# Revit family: pfav-p80_1600dmj1_50Hz.
name_source: partatom
category: 機械設備
units: mm (PartAtom-declared; Revit-internal decimal feet)

## family parameters
OmniClass タイトル = Split System Air Conditioning Units
OmniClass 番号 = 23.75.10.24.21.27.27
パーツ タイプ = 標準
ロード時にボイドで切り取り = いいえ
丸型コネクタ寸法 = 直径を使用
作業面ベース = いいえ
共有 = いいえ
常に垂直 = はい
部屋計算ポイント = いいえ

## types (11) — shared parameters
Clearance Back = 50  [stored 0.164042 ft]
Clearance Right = 100  [stored 0.328084 ft]
Clearance Top = 1000  [stored 3.28084 ft]
IfcExportAs = IfcUnitaryEquipmentType
IfcExportType = AIRCONDITIONINGUNIT
OmniClassCode = 23-33 17 13 11
S寸法 = 150
URL = https://www.mitsubishielectric.co.jp
Uniclass2015Code = Pr_70_65_03_84
Uniclass2015Title = Split coil remote air cooled condensing units
Uniclass2015Version = Systems v1.9
サービススペース = はい
仕様書バージョン = Version1.0
企業コード = 108420
冷媒管径 = 100.00 mm
冷媒高低圧ガス管径 = 0.00 mm
分類コード = 50053003023020
加湿給水管径 = 27.00 mm
参照している仕様書等のバージョン = 公共建築工事標準仕様書（機械設備工事編）平成31年度版
周波数 = 50 Hz
呼称 = パッケージ形空気調和機_室内機
始動方式 = 直入
形式 = 床置（露出）立形
本体マテリアル = <カテゴリ別>
極数 = 3
機外静圧 = 30.0 Pa
法定耐用年数 = 15
消費電力_加湿器 = 0 W
消費電力_電気ヒーター = 0 W
相 = 3
相_電気ヒーター = 1
積算_科目 = 1 空気調和設備
符号 = PAC-FRV(J)
製品リリース年月 = 2017年4月18日
製品出荷対象 = 国内
製造元 = 三菱電機株式会社
設置方法 = 床置形
説明 = 設備用パッケージエアコン 空冷床置形・冷暖兼用 ファシレアＤＤ
負荷分類 = 3_ファン類
運転質量 = 0.00 kg
電動機出力_圧縮機 = 0 W
電圧 = 200 V
電圧_電気ヒーター = 0 V
zero-valued in all types: APF, COP, 価格, 有効加湿量, 機械基礎_D, 機械基礎_H, 機械基礎_W

## per-type parameters (varying)
- PFAV-P80DMJ1: Clearance Front=800  [stored 2.62467 ft]; Clearance Left=500  [stored 1.64042 ft]; Depth=485  [stored 1.59121 ft]; Height=1730  [stored 5.67585 ft]; MAX風量=1620.0 m³/h; Width=760; ダクト幅=383 mm; ダクト高=334 mm; ドレン管径=34.00 mm; 冷媒ガス管径=15.88 mm; 冷媒液管径=9.52 mm; 冷媒管径符号=Bd; 冷房能力=7 kW; 形名=PFAV-P-DMJ : PFAV-P80DMJ1; 推奨ブレーカー容量=15 A; 暖房能力=8 kW; 最大電流値=5 A; 最小電線太さ_mm2=1.6; 消費電力=150 W; 消費電力_冷房=150 W; 消費電力_暖房=150 W; 製品質量=121.00 kg; 質量=145.20 kg; 電動機出力_送風機=1200 W; 音響パワーレベル(dB)=61; 風量=1620.0 m³/h; 風量（m3／min）=27
- PFAV-P280DMJ1: Clearance Front=800  [stored 2.62467 ft]; Clearance Left=500  [stored 1.64042 ft]; Depth=485  [stored 1.59121 ft]; Height=1730  [stored 5.67585 ft]; MAX風量=5400.0 m³/h; Width=980  [stored 3.21522 ft]; ダクト幅=715 mm; ダクト高=334 mm; ドレン管径=34.00 mm; 冷媒ガス管径=22.20 mm; 冷媒液管径=9.52 mm; 冷媒管径符号=Bf; 冷房能力=25 kW; 形名=PFAV-P-DMJ : PFAV-P280DMJ1; 推奨ブレーカー容量=15 A; 暖房能力=28 kW; 最大電流値=6 A; 最小電線太さ_mm2=1.6; 消費電力=1150 W; 消費電力_冷房=1150 W; 消費電力_暖房=1150 W; 製品質量=140.00 kg; 質量=168.00 kg; 電動機出力_送風機=1200 W; 音響パワーレベル(dB)=76; 風量=5400.0 m³/h; 風量（m3／min）=90
- PFAV-P450DMJ1: Clearance Front=1000  [stored 3.28084 ft]; Clearance Left=100  [stored 0.328084 ft]; Depth=635; Height=1897  [stored 6.22375 ft]; MAX風量=8400.0 m³/h; Width=1200; ダクト幅=1046 mm; ダクト高=489 mm; ドレン管径=34.00 mm; 冷媒ガス管径=28.58 mm; 冷媒液管径=15.88 mm; 冷媒管径符号=Dh; 冷房能力=40 kW; 形名=PFAV-P-DMJ : PFAV-P450DMJ1; 推奨ブレーカー容量=15 A; 暖房能力=45 kW; 最大電流値=10 A; 最小電線太さ_mm2=1.6; 消費電力=1310 W; 消費電力_冷房=1310 W; 消費電力_暖房=1310 W; 製品質量=240.00 kg; 質量=288.00 kg; 電動機出力_送風機=2400 W; 音響パワーレベル(dB)=75; 風量=8400.0 m³/h; 風量（m3／min）=140
- PFAV-P140DMJ1: Clearance Front=800  [stored 2.62467 ft]; Clearance Left=500  [stored 1.64042 ft]; Depth=485  [stored 1.59121 ft]; Height=1730  [stored 5.67585 ft]; MAX風量=2700.0 m³/h; Width=760; ダクト幅=383 mm; ダクト高=334 mm; ドレン管径=34.00 mm; 冷媒ガス管径=15.88 mm; 冷媒液管径=9.52 mm; 冷媒管径符号=Bd; 冷房能力=13 kW; 形名=PFAV-P-DMJ : PFAV-P140DMJ1; 推奨ブレーカー容量=15 A; 暖房能力=14 kW; 最大電流値=5 A; 最小電線太さ_mm2=1.6; 消費電力=410 W; 消費電力_冷房=410 W; 消費電力_暖房=410 W; 製品質量=136.00 kg; 質量=163.20 kg; 電動機出力_送風機=1200 W; 音響パワーレベル(dB)=68; 風量=2700.0 m³/h; 風量（m3／min）=45
- PFAV-P224DMJ1: Clearance Front=800  [stored 2.62467 ft]; Clearance Left=500  [stored 1.64042 ft]; Depth=485  [stored 1.59121 ft]; Height=1730  [stored 5.67585 ft]; MAX風量=3900.0 m³/h; Width=980  [stored 3.21522 ft]; ダクト幅=715 mm; ダクト高=334 mm; ドレン管径=34.00 mm; 冷媒ガス管径=19.05 mm; 冷媒液管径=9.52 mm; 冷媒管径符号=Be; 冷房能力=20 kW; 形名=PFAV-P-DMJ : PFAV-P224DMJ1; 推奨ブレーカー容量=15 A; 暖房能力=22 kW; 最大電流値=6 A; 最小電線太さ_mm2=1.6; 消費電力=510 W; 消費電力_冷房=510 W; 消費電力_暖房=510 W; 製品質量=136.00 kg; 質量=163.20 kg; 電動機出力_送風機=1200 W; 音響パワーレベル(dB)=68; 風量=3900.0 m³/h; 風量（m3／min）=65
- PFAV-P560DMJ1: Clearance Front=1000  [stored 3.28084 ft]; Clearance Left=100  [stored 0.328084 ft]; Depth=635; Height=1897  [stored 6.22375 ft]; MAX風量=9900.0 m³/h; Width=1200; ダクト幅=1046 mm; ダクト高=489 mm; ドレン管径=34.00 mm; 冷媒ガス管径=28.58 mm; 冷媒液管径=15.88 mm; 冷媒管径符号=Dh; 冷房能力=50 kW; 形名=PFAV-P-DMJ : PFAV-P560DMJ1; 推奨ブレーカー容量=15 A; 暖房能力=56 kW; 最大電流値=10 A; 最小電線太さ_mm2=1.6; 消費電力=1690 W; 消費電力_冷房=1690 W; 消費電力_暖房=1690 W; 製品質量=240.00 kg; 質量=288.00 kg; 電動機出力_送風機=2400 W; 音響パワーレベル(dB)=78; 風量=9900.0 m³/h; 風量（m3／min）=165
- PFAV-P670DMJ1: Clearance Front=1000  [stored 3.28084 ft]; Clearance Left=100  [stored 0.328084 ft]; Depth=1064  [stored 3.49081 ft]; Height=1830  [stored 6.00394 ft]; MAX風量=12600.0 m³/h; Width=1750  [stored 5.74147 ft]; ダクト幅=677 mm; ダクト高=484 mm; ドレン管径=42.70 mm; 冷媒ガス管径=28.58 mm; 冷媒液管径=15.88 mm; 冷媒管径符号=Dh; 冷房能力=63 kW; 形名=PFAV-P-DMJ : PFAV-P670DMJ1; 推奨ブレーカー容量=40 A; 暖房能力=63 kW; 最大電流値=21 A; 最小電線太さ_mm2=5.5; 消費電力=2140 W; 消費電力_冷房=2140 W; 消費電力_暖房=2140 W; 製品質量=418.00 kg; 質量=501.60 kg; 電動機出力_送風機=7500 W; 音響パワーレベル(dB)=77; 風量=12600.0 m³/h; 風量（m3／min）=210
- PFAV-P800DMJ1: Clearance Front=1000  [stored 3.28084 ft]; Clearance Left=100  [stored 0.328084 ft]; Depth=1064  [stored 3.49081 ft]; Height=1830  [stored 6.00394 ft]; MAX風量=15600.0 m³/h; Width=1750  [stored 5.74147 ft]; ダクト幅=677 mm; ダクト高=484 mm; ドレン管径=42.70 mm; 冷媒ガス管径=31.75 mm; 冷媒液管径=19.05 mm; 冷媒管径符号=Ei; 冷房能力=71 kW; 形名=PFAV-P-DMJ : PFAV-P800DMJ1; 推奨ブレーカー容量=40 A; 暖房能力=80 kW; 最大電流値=21 A; 最小電線太さ_mm2=5.5; 消費電力=3640 W; 消費電力_冷房=3640 W; 消費電力_暖房=3640 W; 製品質量=424.00 kg; 質量=508.80 kg; 電動機出力_送風機=7500 W; 音響パワーレベル(dB)=82; 風量=15600.0 m³/h; 風量（m3／min）=260
- PFAV-P1120DMJ1: Clearance Front=1000  [stored 3.28084 ft]; Clearance Left=100  [stored 0.328084 ft]; Depth=1064  [stored 3.49081 ft]; Height=1830  [stored 6.00394 ft]; MAX風量=20400.0 m³/h; Width=1750  [stored 5.74147 ft]; ダクト幅=677 mm; ダクト高=484 mm; ドレン管径=42.70 mm; 冷媒ガス管径=38.10 mm; 冷媒液管径=19.05 mm; 冷媒管径符号=Ek; 冷房能力=100 kW; 形名=PFAV-P-DMJ : PFAV-P1120DMJ1; 推奨ブレーカー容量=50 A; 暖房能力=112 kW; 最大電流値=32 A; 最小電線太さ_mm2=8; 消費電力=5960 W; 消費電力_冷房=5960 W; 消費電力_暖房=5960 W; 製品質量=473.00 kg; 質量=567.60 kg; 電動機出力_送風機=11000 W; 音響パワーレベル(dB)=85; 風量=20400.0 m³/h; 風量（m3／min）=340
- PFAV-P1400DMJ1: Clearance Front=1000  [stored 3.28084 ft]; Clearance Left=100  [stored 0.328084 ft]; Depth=1064  [stored 3.49081 ft]; Height=1830  [stored 6.00394 ft]; MAX風量=27000.0 m³/h; Width=2045  [stored 6.70932 ft]; ダクト幅=1806 mm; ダクト高=520 mm; ドレン管径=42.70 mm; 冷媒ガス管径=38.10 mm; 冷媒液管径=19.05 mm; 冷媒管径符号=Ek; 冷房能力=122 kW; 形名=PFAV-P-DMJ : PFAV-P1400DMJ1; 推奨ブレーカー容量=75 A; 暖房能力=140 kW; 最大電流値=42 A; 最小電線太さ_mm2=14; 消費電力=6090 W; 消費電力_冷房=6090 W; 消費電力_暖房=6090 W; 製品質量=649.00 kg; 質量=778.80 kg; 電動機出力_送風機=15000 W; 音響パワーレベル(dB)=77; 風量=27000.0 m³/h; 風量（m3／min）=450
- PFAV-P1600DMJ1: Clearance Front=1000  [stored 3.28084 ft]; Clearance Left=100  [stored 0.328084 ft]; Depth=1064  [stored 3.49081 ft]; Height=1830  [stored 6.00394 ft]; MAX風量=31200.0 m³/h; Width=2045  [stored 6.70932 ft]; ダクト幅=1806 mm; ダクト高=520 mm; ドレン管径=42.70 mm; 冷媒ガス管径=31.75 mm; 冷媒液管径=19.05 mm; 冷媒管径符号=Ei; 冷房能力=140 kW; 形名=PFAV-P-DMJ : PFAV-P1600DMJ1; 推奨ブレーカー容量=75 A; 暖房能力=160 kW; 最大電流値=65 A; 最小電線太さ_mm2=22; 消費電力=8420 W; 消費電力_冷房=8420 W; 消費電力_暖房=8420 W; 製品質量=722.00 kg; 質量=866.40 kg; 電動機出力_送風機=22000 W; 音響パワーレベル(dB)=79; 風量=31200.0 m³/h; 風量（m3／min）=520

note: column(s) folded — value = type name in every type: モデル

note: [stored X ft] marks values corroborated as IEEE doubles in the binary element streams (Revit-internal decimal feet)

## geometry (parser evidence)
native form markers: Blend x4
no freeform markers — native parametric forms only
